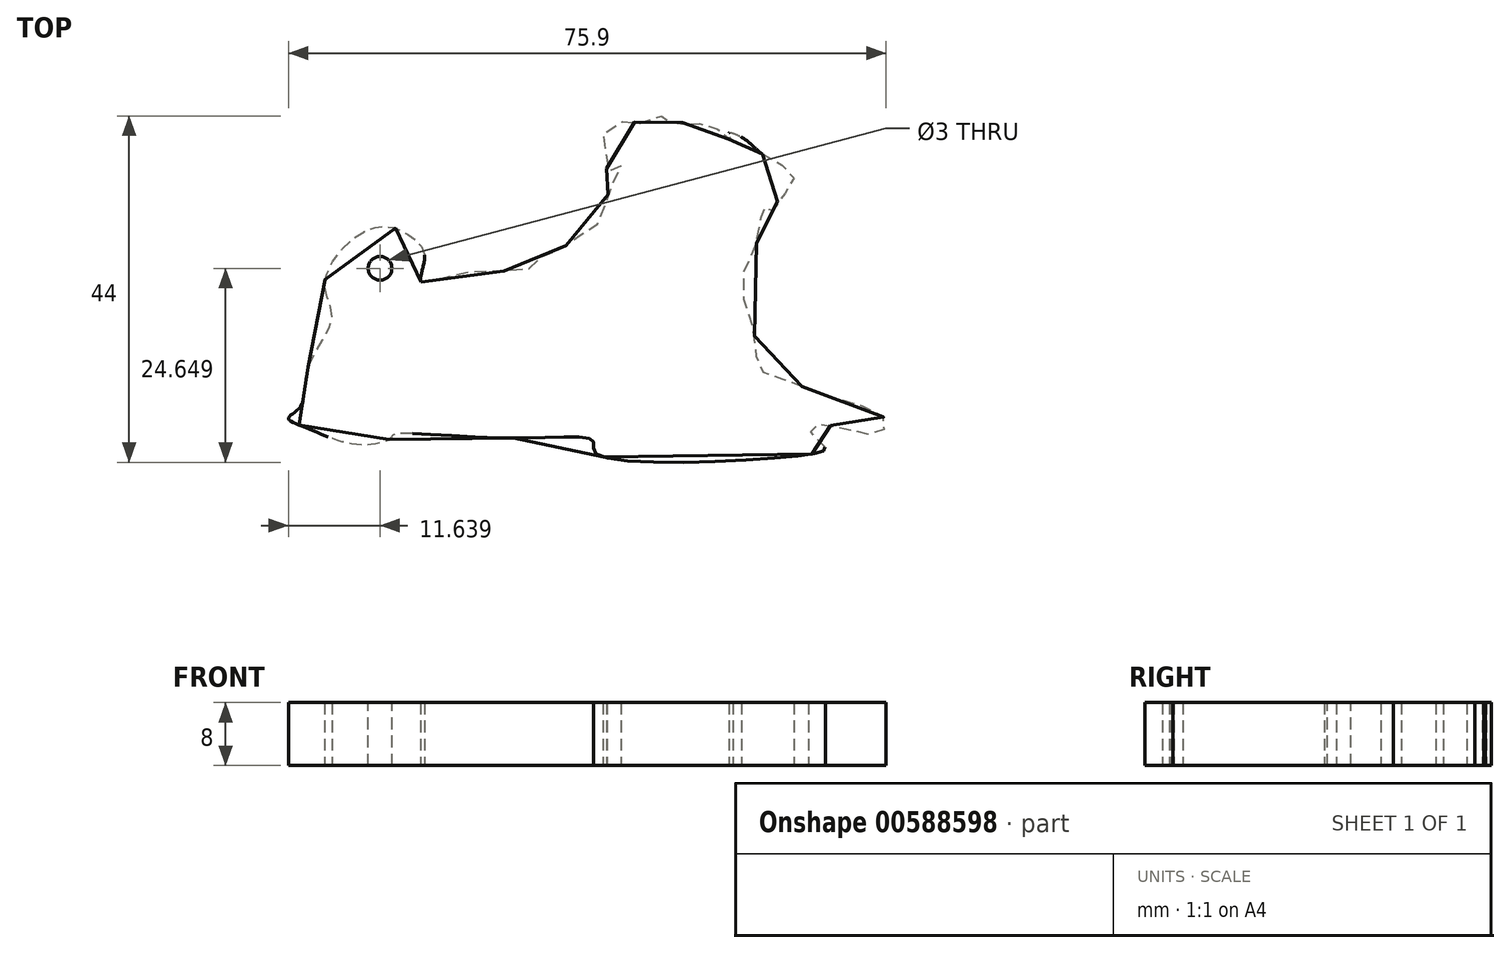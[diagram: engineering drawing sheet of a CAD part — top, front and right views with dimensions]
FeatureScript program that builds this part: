
annotation { "Feature Type Name" : "Feature", "Feature Type Description" : "" }
export const myFeature = defineFeature(function(context is Context, id is Id, definition is map)
    precondition{}
    {
        {
            var Q0;
            Q0=qCreatedBy(makeId("Top.planeOp"),FACE);
            var sketch = newSketch(context, id + "F0", { "sketchPlane" : qUnion([Q0])});
            skFitSpline(sketch, "E0", {"points": [v(-60.71, 33.2) * mm, v(-57.19, 33.94) * mm, v(-52.28, 34.58) * mm, v(-46.72, 35) * mm, v(-45.55, 36.29) * mm, v(-42.67, 37.57) * mm, v(-40.1, 39.38) * mm, v(-37.86, 41.1) * mm, v(-36.9, 44.61) * mm, v(-35.83, 46.54) * mm, v(-35.4, 48.14) * mm, v(-37, 47.18) * mm, v(-37.12, 48.88) * mm, v(-37.44, 52.3) * mm, v(-34.23, 53.58) * mm, v(-32.53, 53.37) * mm, v(-29.86, 54.22) * mm, v(-29.43, 53.58) * mm, v(-27.61, 53.48) * mm, v(-27.19, 53.16) * mm, v(-25.7, 53.26) * mm, v(-23.34, 52.84) * mm, v(-21.74, 51.34) * mm, v(-21.1, 51.23) * mm, v(-21.64, 52.09) * mm, v(-19.82, 51.45) * mm, v(-17.37, 49.42) * mm, v(-13.84, 47.28) * mm, v(-13.52, 45.68) * mm, v(-15.76, 42.9) * mm, v(-16.51, 41.84) * mm, v(-17.37, 42.8) * mm, v(-17.8, 39.28) * mm, v(-20.03, 33.3) * mm, v(-18.54, 27.1) * mm, v(-17.8, 22.2) * mm, v(-15.87, 21.23) * mm, v(-9.57, 18.89) * mm, v(-4.55, 17.4) * mm, v(-1.78, 15.68) * mm, v(-2.1, 14.3) * mm, v(-4.34, 13.87) * mm, v(-9.57, 15.04) * mm, v(-11.5, 14.5) * mm, v(-9.47, 12.27) * mm, v(-11.81, 11.2) * mm, v(-38.61, 11.41) * mm, v(-38.82, 12.9) * mm, v(-49.18, 13.33) * mm, v(-64.23, 13.76) * mm, v(-64.55, 13.33) * mm, v(-68.5, 12.48) * mm, v(-75.02, 14.5) * mm, v(-77.58, 15.9) * mm, v(-76.08, 17.28) * mm, v(-75.12, 22.2) * mm, v(-72.03, 28.7) * mm, v(-72.99, 32.98) * mm, v(-68.5, 39.28) * mm, v(-64.45, 40.13) * mm, v(-62.2, 39.06) * mm, v(-60.28, 36.6) * mm, v(-60.71, 33.2) * mm]});
            skSolve(sketch);
        }
        {
            var Q0;
            Q0 = qSketchRegion(id + "F0", true);
            extrude(context, id + "F1", {"entities" : qUnion([Q0]), "depth" : 8 * mm, "offsetDistance" : 25 * mm});
        }
        {
            var Q0;
            Q0=makeQuery(id+"F1.opExtrude","CAP_FACE",FACE,{"disambiguationData":[OSD([sQuery(id+"F0.wireOp",EDGE,"E0")])],"isStart":false});
            var sketch = newSketch(context, id + "F2", { "sketchPlane" : qUnion([Q0])});
            skPoint(sketch, "E1", {"position": v(-65.94, 34.9) * mm});
            skSolve(sketch);
        }
        {
            var Q0;
            Q0=sQuery(id+"F2.wireOp",VERTEX,"E1");
            var Q1;
            Q1=makeQuery(id+"F1.opExtrude","SWEPT_BODY",BODY,{"disambiguationData":[OSD([sQuery(id+"F0.wireOp",EDGE,"E0")])]});
            hole(context, id + "F3", {"style" : HoleStyle.SIMPLE, "endStyle" : HoleEndStyle.THROUGH, "holeDiameter" : 3 * mm, "majorDiameter" : 5 * mm, "isTappedThrough" : true, "tappedDepth" : 12 * mm, "tapClearance" : 3, "locations" : qUnion([Q0]), "scope" : qUnion([Q1])});
        }
    });
